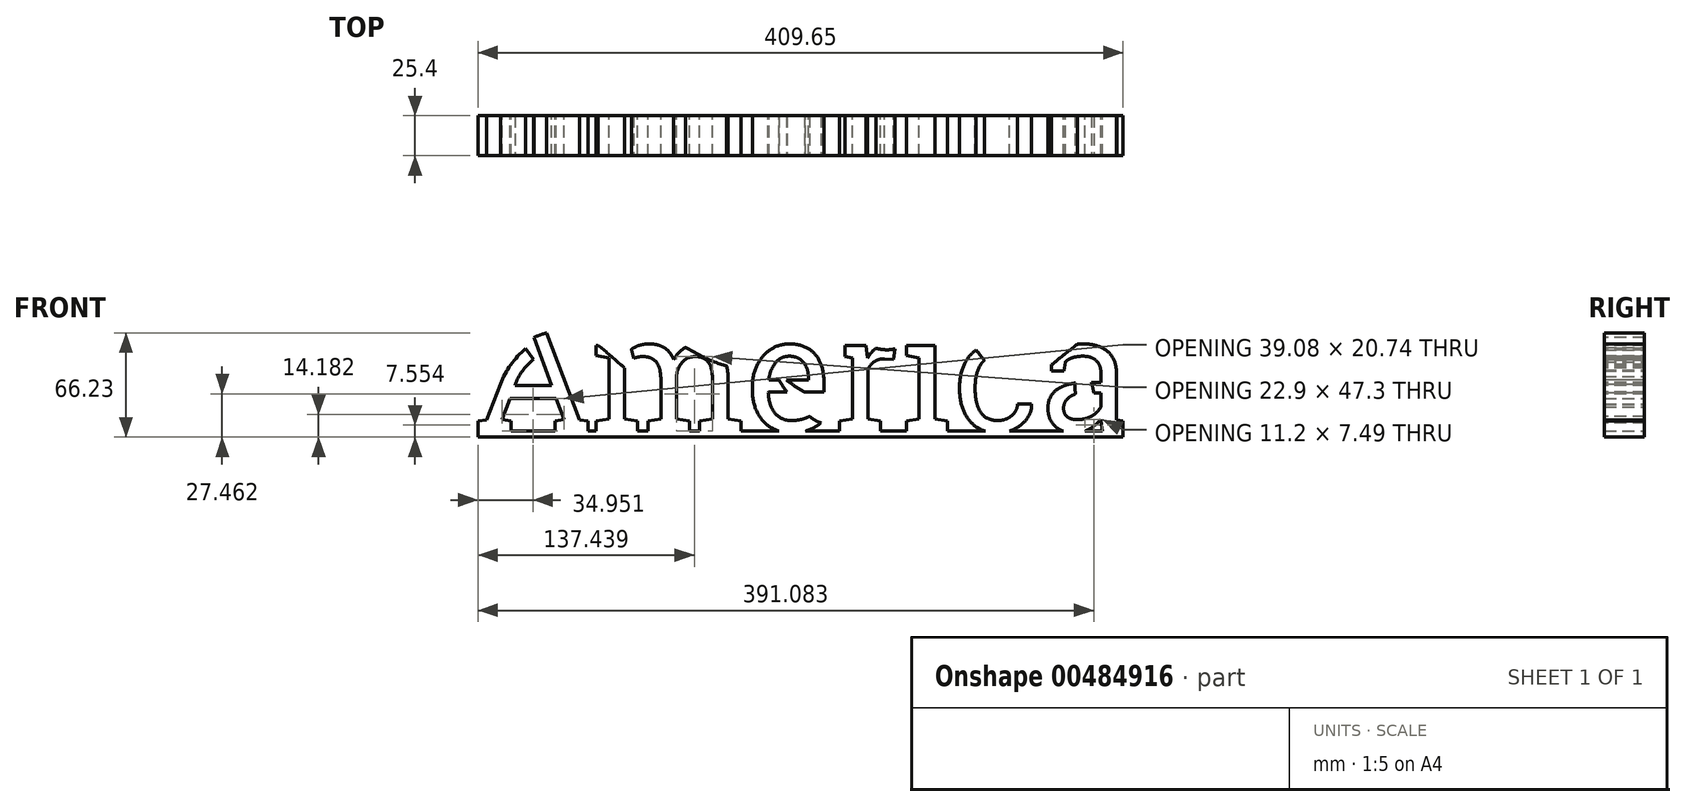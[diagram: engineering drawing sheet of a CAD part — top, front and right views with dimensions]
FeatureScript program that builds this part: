
annotation { "Feature Type Name" : "Feature", "Feature Type Description" : "" }
export const myFeature = defineFeature(function(context is Context, id is Id, definition is map)
    precondition{}
    {
        {
            var Q0;
            Q0=qCreatedBy(makeId("Front.planeOp"),FACE);
            var sketch = newSketch(context, id + "F0", { "sketchPlane" : qUnion([Q0])});
            skText(sketch, "E0", { "text": "America", "fontName": "RobotoSlab-Regular.ttf"});
            const initialGuessF0  = {"E0": [-0.10996, 0, 1, 0, 0.07404]};
            skSetInitialGuess(sketch, initialGuessF0);
            skSolve(sketch);
        }
        {
            var Q0;
            Q0 = qSketchRegion(id + "F0", true);
            extrude(context, id + "F1", {"entities" : qUnion([Q0]), "depth" : 25.4 * mm});
        }
        {
            var Q0;
            Q0=makeQuery(id+"F1.opExtrude","SWEPT_FACE",FACE,{"disambiguationData":[OSD([sQuery(id+"F0.wireOp",EDGE,"E0.sketch_text.stroke-14")])]});
            var sketch = newSketch(context, id + "F2", { "sketchPlane" : qUnion([Q0])});
            skLineSegment(sketch, "E1.bottom", {"start": v(-107.2, 25.4) * mm, "end": v(302.44, 25.4) * mm});
            skLineSegment(sketch, "E1.top", {"start": v(-107.2, 0) * mm, "end": v(302.44, 0) * mm});
            skLineSegment(sketch, "E1.left", {"start": v(-107.2, 25.4) * mm, "end": v(-107.2, 0) * mm});
            skLineSegment(sketch, "E1.right", {"start": v(302.44, 25.4) * mm, "end": v(302.44, 0) * mm});
            skSolve(sketch);
        }
        {
            var Q0;
            Q0 = qSketchRegion(id + "F2", true);
            extrude(context, id + "F3", {"entities" : qUnion([Q0]), "operationType" : NewBodyOperationType.ADD, "depth" : 3.8 * mm});
        }
        {
            var Q0;
            Q0=makeQuery(id+"F3.boolean.opBoolean","MERGE",FACE,{"derivedFrom":[makeQuery(id+"F1.opExtrude","CAP_FACE",FACE,{"disambiguationData":[OSD([sQuery(id+"F0.wireOp",EDGE,"E0.sketch_text.stroke-0"),sQuery(id+"F0.wireOp",EDGE,"E0.sketch_text.stroke-1"),sQuery(id+"F0.wireOp",EDGE,"E0.sketch_text.stroke-2"),sQuery(id+"F0.wireOp",EDGE,"E0.sketch_text.stroke-3"),sQuery(id+"F0.wireOp",EDGE,"E0.sketch_text.stroke-4"),sQuery(id+"F0.wireOp",EDGE,"E0.sketch_text.stroke-5"),sQuery(id+"F0.wireOp",EDGE,"E0.sketch_text.stroke-6"),sQuery(id+"F0.wireOp",EDGE,"E0.sketch_text.stroke-7"),sQuery(id+"F0.wireOp",EDGE,"E0.sketch_text.stroke-8"),sQuery(id+"F0.wireOp",EDGE,"E0.sketch_text.stroke-9"),sQuery(id+"F0.wireOp",EDGE,"E0.sketch_text.stroke-10"),sQuery(id+"F0.wireOp",EDGE,"E0.sketch_text.stroke-11"),sQuery(id+"F0.wireOp",EDGE,"E0.sketch_text.stroke-12"),sQuery(id+"F0.wireOp",EDGE,"E0.sketch_text.stroke-13"),sQuery(id+"F0.wireOp",EDGE,"E0.sketch_text.stroke-14"),sQuery(id+"F0.wireOp",EDGE,"E0.sketch_text.stroke-15"),sQuery(id+"F0.wireOp",EDGE,"E0.sketch_text.stroke-16"),sQuery(id+"F0.wireOp",EDGE,"E0.sketch_text.stroke-17"),sQuery(id+"F0.wireOp",EDGE,"E0.sketch_text.stroke-18"),sQuery(id+"F0.wireOp",EDGE,"E0.sketch_text.stroke-19")])],"isStart":false}),makeQuery(id+"F1.opExtrude","CAP_FACE",FACE,{"disambiguationData":[OSD([sQuery(id+"F0.wireOp",EDGE,"E0.sketch_text.stroke-20"),sQuery(id+"F0.wireOp",EDGE,"E0.sketch_text.stroke-21"),sQuery(id+"F0.wireOp",EDGE,"E0.sketch_text.stroke-22"),sQuery(id+"F0.wireOp",EDGE,"E0.sketch_text.stroke-23"),sQuery(id+"F0.wireOp",EDGE,"E0.sketch_text.stroke-24"),sQuery(id+"F0.wireOp",EDGE,"E0.sketch_text.stroke-25"),sQuery(id+"F0.wireOp",EDGE,"E0.sketch_text.stroke-26"),sQuery(id+"F0.wireOp",EDGE,"E0.sketch_text.stroke-27"),sQuery(id+"F0.wireOp",EDGE,"E0.sketch_text.stroke-28"),sQuery(id+"F0.wireOp",EDGE,"E0.sketch_text.stroke-29"),sQuery(id+"F0.wireOp",EDGE,"E0.sketch_text.stroke-30"),sQuery(id+"F0.wireOp",EDGE,"E0.sketch_text.stroke-31"),sQuery(id+"F0.wireOp",EDGE,"E0.sketch_text.stroke-32"),sQuery(id+"F0.wireOp",EDGE,"E0.sketch_text.stroke-33"),sQuery(id+"F0.wireOp",EDGE,"E0.sketch_text.stroke-34"),sQuery(id+"F0.wireOp",EDGE,"E0.sketch_text.stroke-35"),sQuery(id+"F0.wireOp",EDGE,"E0.sketch_text.stroke-36"),sQuery(id+"F0.wireOp",EDGE,"E0.sketch_text.stroke-37"),sQuery(id+"F0.wireOp",EDGE,"E0.sketch_text.stroke-38"),sQuery(id+"F0.wireOp",EDGE,"E0.sketch_text.stroke-39"),sQuery(id+"F0.wireOp",EDGE,"E0.sketch_text.stroke-40"),sQuery(id+"F0.wireOp",EDGE,"E0.sketch_text.stroke-41"),sQuery(id+"F0.wireOp",EDGE,"E0.sketch_text.stroke-42"),sQuery(id+"F0.wireOp",EDGE,"E0.sketch_text.stroke-43"),sQuery(id+"F0.wireOp",EDGE,"E0.sketch_text.stroke-44"),sQuery(id+"F0.wireOp",EDGE,"E0.sketch_text.stroke-45"),sQuery(id+"F0.wireOp",EDGE,"E0.sketch_text.stroke-46"),sQuery(id+"F0.wireOp",EDGE,"E0.sketch_text.stroke-47"),sQuery(id+"F0.wireOp",EDGE,"E0.sketch_text.stroke-48"),sQuery(id+"F0.wireOp",EDGE,"E0.sketch_text.stroke-49"),sQuery(id+"F0.wireOp",EDGE,"E0.sketch_text.stroke-50"),sQuery(id+"F0.wireOp",EDGE,"E0.sketch_text.stroke-51"),sQuery(id+"F0.wireOp",EDGE,"E0.sketch_text.stroke-52"),sQuery(id+"F0.wireOp",EDGE,"E0.sketch_text.stroke-53"),sQuery(id+"F0.wireOp",EDGE,"E0.sketch_text.stroke-54"),sQuery(id+"F0.wireOp",EDGE,"E0.sketch_text.stroke-55"),sQuery(id+"F0.wireOp",EDGE,"E0.sketch_text.stroke-56"),sQuery(id+"F0.wireOp",EDGE,"E0.sketch_text.stroke-57"),sQuery(id+"F0.wireOp",EDGE,"E0.sketch_text.stroke-58"),sQuery(id+"F0.wireOp",EDGE,"E0.sketch_text.stroke-59"),sQuery(id+"F0.wireOp",EDGE,"E0.sketch_text.stroke-60")])],"isStart":false}),makeQuery(id+"F1.opExtrude","CAP_FACE",FACE,{"disambiguationData":[OSD([sQuery(id+"F0.wireOp",EDGE,"E0.sketch_text.stroke-61"),sQuery(id+"F0.wireOp",EDGE,"E0.sketch_text.stroke-62"),sQuery(id+"F0.wireOp",EDGE,"E0.sketch_text.stroke-63"),sQuery(id+"F0.wireOp",EDGE,"E0.sketch_text.stroke-64"),sQuery(id+"F0.wireOp",EDGE,"E0.sketch_text.stroke-65"),sQuery(id+"F0.wireOp",EDGE,"E0.sketch_text.stroke-66"),sQuery(id+"F0.wireOp",EDGE,"E0.sketch_text.stroke-67"),sQuery(id+"F0.wireOp",EDGE,"E0.sketch_text.stroke-68"),sQuery(id+"F0.wireOp",EDGE,"E0.sketch_text.stroke-69"),sQuery(id+"F0.wireOp",EDGE,"E0.sketch_text.stroke-70"),sQuery(id+"F0.wireOp",EDGE,"E0.sketch_text.stroke-71"),sQuery(id+"F0.wireOp",EDGE,"E0.sketch_text.stroke-72"),sQuery(id+"F0.wireOp",EDGE,"E0.sketch_text.stroke-73"),sQuery(id+"F0.wireOp",EDGE,"E0.sketch_text.stroke-74"),sQuery(id+"F0.wireOp",EDGE,"E0.sketch_text.stroke-75"),sQuery(id+"F0.wireOp",EDGE,"E0.sketch_text.stroke-76"),sQuery(id+"F0.wireOp",EDGE,"E0.sketch_text.stroke-77"),sQuery(id+"F0.wireOp",EDGE,"E0.sketch_text.stroke-78"),sQuery(id+"F0.wireOp",EDGE,"E0.sketch_text.stroke-79"),sQuery(id+"F0.wireOp",EDGE,"E0.sketch_text.stroke-80"),sQuery(id+"F0.wireOp",EDGE,"E0.sketch_text.stroke-81"),sQuery(id+"F0.wireOp",EDGE,"E0.sketch_text.stroke-82"),sQuery(id+"F0.wireOp",EDGE,"E0.sketch_text.stroke-83"),sQuery(id+"F0.wireOp",EDGE,"E0.sketch_text.stroke-84")])],"isStart":false}),makeQuery(id+"F1.opExtrude","CAP_FACE",FACE,{"disambiguationData":[OSD([sQuery(id+"F0.wireOp",EDGE,"E0.sketch_text.stroke-85"),sQuery(id+"F0.wireOp",EDGE,"E0.sketch_text.stroke-86"),sQuery(id+"F0.wireOp",EDGE,"E0.sketch_text.stroke-87"),sQuery(id+"F0.wireOp",EDGE,"E0.sketch_text.stroke-88"),sQuery(id+"F0.wireOp",EDGE,"E0.sketch_text.stroke-89"),sQuery(id+"F0.wireOp",EDGE,"E0.sketch_text.stroke-90"),sQuery(id+"F0.wireOp",EDGE,"E0.sketch_text.stroke-91"),sQuery(id+"F0.wireOp",EDGE,"E0.sketch_text.stroke-92"),sQuery(id+"F0.wireOp",EDGE,"E0.sketch_text.stroke-93"),sQuery(id+"F0.wireOp",EDGE,"E0.sketch_text.stroke-94"),sQuery(id+"F0.wireOp",EDGE,"E0.sketch_text.stroke-95"),sQuery(id+"F0.wireOp",EDGE,"E0.sketch_text.stroke-96"),sQuery(id+"F0.wireOp",EDGE,"E0.sketch_text.stroke-97"),sQuery(id+"F0.wireOp",EDGE,"E0.sketch_text.stroke-98"),sQuery(id+"F0.wireOp",EDGE,"E0.sketch_text.stroke-99"),sQuery(id+"F0.wireOp",EDGE,"E0.sketch_text.stroke-100"),sQuery(id+"F0.wireOp",EDGE,"E0.sketch_text.stroke-101"),sQuery(id+"F0.wireOp",EDGE,"E0.sketch_text.stroke-102"),sQuery(id+"F0.wireOp",EDGE,"E0.sketch_text.stroke-103")])],"isStart":false}),makeQuery(id+"F1.opExtrude","CAP_FACE",FACE,{"disambiguationData":[OSD([sQuery(id+"F0.wireOp",EDGE,"E0.sketch_text.stroke-104"),sQuery(id+"F0.wireOp",EDGE,"E0.sketch_text.stroke-105"),sQuery(id+"F0.wireOp",EDGE,"E0.sketch_text.stroke-106"),sQuery(id+"F0.wireOp",EDGE,"E0.sketch_text.stroke-107"),sQuery(id+"F0.wireOp",EDGE,"E0.sketch_text.stroke-108"),sQuery(id+"F0.wireOp",EDGE,"E0.sketch_text.stroke-109"),sQuery(id+"F0.wireOp",EDGE,"E0.sketch_text.stroke-110"),sQuery(id+"F0.wireOp",EDGE,"E0.sketch_text.stroke-111"),sQuery(id+"F0.wireOp",EDGE,"E0.sketch_text.stroke-112"),sQuery(id+"F0.wireOp",EDGE,"E0.sketch_text.stroke-113")])],"isStart":false}),makeQuery(id+"F1.opExtrude","CAP_FACE",FACE,{"disambiguationData":[OSD([sQuery(id+"F0.wireOp",EDGE,"E0.sketch_text.stroke-118"),sQuery(id+"F0.wireOp",EDGE,"E0.sketch_text.stroke-119"),sQuery(id+"F0.wireOp",EDGE,"E0.sketch_text.stroke-120"),sQuery(id+"F0.wireOp",EDGE,"E0.sketch_text.stroke-121"),sQuery(id+"F0.wireOp",EDGE,"E0.sketch_text.stroke-122"),sQuery(id+"F0.wireOp",EDGE,"E0.sketch_text.stroke-123"),sQuery(id+"F0.wireOp",EDGE,"E0.sketch_text.stroke-124"),sQuery(id+"F0.wireOp",EDGE,"E0.sketch_text.stroke-125"),sQuery(id+"F0.wireOp",EDGE,"E0.sketch_text.stroke-126"),sQuery(id+"F0.wireOp",EDGE,"E0.sketch_text.stroke-127"),sQuery(id+"F0.wireOp",EDGE,"E0.sketch_text.stroke-128"),sQuery(id+"F0.wireOp",EDGE,"E0.sketch_text.stroke-129"),sQuery(id+"F0.wireOp",EDGE,"E0.sketch_text.stroke-130"),sQuery(id+"F0.wireOp",EDGE,"E0.sketch_text.stroke-131"),sQuery(id+"F0.wireOp",EDGE,"E0.sketch_text.stroke-132"),sQuery(id+"F0.wireOp",EDGE,"E0.sketch_text.stroke-133"),sQuery(id+"F0.wireOp",EDGE,"E0.sketch_text.stroke-134"),sQuery(id+"F0.wireOp",EDGE,"E0.sketch_text.stroke-135"),sQuery(id+"F0.wireOp",EDGE,"E0.sketch_text.stroke-136"),sQuery(id+"F0.wireOp",EDGE,"E0.sketch_text.stroke-137"),sQuery(id+"F0.wireOp",EDGE,"E0.sketch_text.stroke-138"),sQuery(id+"F0.wireOp",EDGE,"E0.sketch_text.stroke-139"),sQuery(id+"F0.wireOp",EDGE,"E0.sketch_text.stroke-140")])],"isStart":false}),makeQuery(id+"F1.opExtrude","CAP_FACE",FACE,{"disambiguationData":[OSD([sQuery(id+"F0.wireOp",EDGE,"E0.sketch_text.stroke-141"),sQuery(id+"F0.wireOp",EDGE,"E0.sketch_text.stroke-142"),sQuery(id+"F0.wireOp",EDGE,"E0.sketch_text.stroke-143"),sQuery(id+"F0.wireOp",EDGE,"E0.sketch_text.stroke-144"),sQuery(id+"F0.wireOp",EDGE,"E0.sketch_text.stroke-145"),sQuery(id+"F0.wireOp",EDGE,"E0.sketch_text.stroke-146"),sQuery(id+"F0.wireOp",EDGE,"E0.sketch_text.stroke-147"),sQuery(id+"F0.wireOp",EDGE,"E0.sketch_text.stroke-148"),sQuery(id+"F0.wireOp",EDGE,"E0.sketch_text.stroke-149"),sQuery(id+"F0.wireOp",EDGE,"E0.sketch_text.stroke-150"),sQuery(id+"F0.wireOp",EDGE,"E0.sketch_text.stroke-151"),sQuery(id+"F0.wireOp",EDGE,"E0.sketch_text.stroke-152"),sQuery(id+"F0.wireOp",EDGE,"E0.sketch_text.stroke-153"),sQuery(id+"F0.wireOp",EDGE,"E0.sketch_text.stroke-154"),sQuery(id+"F0.wireOp",EDGE,"E0.sketch_text.stroke-155"),sQuery(id+"F0.wireOp",EDGE,"E0.sketch_text.stroke-156"),sQuery(id+"F0.wireOp",EDGE,"E0.sketch_text.stroke-157"),sQuery(id+"F0.wireOp",EDGE,"E0.sketch_text.stroke-158"),sQuery(id+"F0.wireOp",EDGE,"E0.sketch_text.stroke-159"),sQuery(id+"F0.wireOp",EDGE,"E0.sketch_text.stroke-160"),sQuery(id+"F0.wireOp",EDGE,"E0.sketch_text.stroke-161"),sQuery(id+"F0.wireOp",EDGE,"E0.sketch_text.stroke-162"),sQuery(id+"F0.wireOp",EDGE,"E0.sketch_text.stroke-163"),sQuery(id+"F0.wireOp",EDGE,"E0.sketch_text.stroke-164"),sQuery(id+"F0.wireOp",EDGE,"E0.sketch_text.stroke-165"),sQuery(id+"F0.wireOp",EDGE,"E0.sketch_text.stroke-166"),sQuery(id+"F0.wireOp",EDGE,"E0.sketch_text.stroke-167"),sQuery(id+"F0.wireOp",EDGE,"E0.sketch_text.stroke-168"),sQuery(id+"F0.wireOp",EDGE,"E0.sketch_text.stroke-169"),sQuery(id+"F0.wireOp",EDGE,"E0.sketch_text.stroke-170"),sQuery(id+"F0.wireOp",EDGE,"E0.sketch_text.stroke-171"),sQuery(id+"F0.wireOp",EDGE,"E0.sketch_text.stroke-172"),sQuery(id+"F0.wireOp",EDGE,"E0.sketch_text.stroke-173"),sQuery(id+"F0.wireOp",EDGE,"E0.sketch_text.stroke-174"),sQuery(id+"F0.wireOp",EDGE,"E0.sketch_text.stroke-175")])],"isStart":false}),makeQuery(id+"F3.opExtrude","SWEPT_FACE",FACE,{"disambiguationData":[OSD([sQuery(id+"F2.wireOp",EDGE,"E1.bottom")])]})]});
            var sketch = newSketch(context, id + "F4", { "sketchPlane" : qUnion([Q0])});
            skFitSpline(sketch, "E2", {"points": [v(-100.8, 53.9) * mm, v(-46.48, 63.1) * mm, v(-6.63, 35.95) * mm, v(-11.01, 68.8) * mm, v(58.62, 40.33) * mm, v(96.29, 68.36) * mm, v(154.97, 51.72) * mm, v(190, 67.92) * mm, v(230.3, 27.63) * mm, v(248.7, 35.07) * mm, v(294.43, 72.4) * mm, v(304.52, 101.14) * mm, v(-135.8, 109.68) * mm, v(-100.8, 53.9) * mm]});
            skSolve(sketch);
        }
        {
            var Q0;
            Q0 = qSketchRegion(id + "F4", true);
            extrude(context, id + "F5", {"entities" : qUnion([Q0]), "operationType" : NewBodyOperationType.REMOVE, "endBound" : BoundingType.THROUGH_ALL, "oppositeDirection" : true, "depth" : 25.4 * mm});
        }
        {
            var Q0;
            Q0=makeQuery(id+"F3.boolean.opBoolean","MERGE",FACE,{"derivedFrom":[makeQuery(id+"F1.opExtrude","CAP_FACE",FACE,{"disambiguationData":[OSD([sQuery(id+"F0.wireOp",EDGE,"E0.sketch_text.stroke-0"),sQuery(id+"F0.wireOp",EDGE,"E0.sketch_text.stroke-1"),sQuery(id+"F0.wireOp",EDGE,"E0.sketch_text.stroke-2"),sQuery(id+"F0.wireOp",EDGE,"E0.sketch_text.stroke-3"),sQuery(id+"F0.wireOp",EDGE,"E0.sketch_text.stroke-4"),sQuery(id+"F0.wireOp",EDGE,"E0.sketch_text.stroke-5"),sQuery(id+"F0.wireOp",EDGE,"E0.sketch_text.stroke-6"),sQuery(id+"F0.wireOp",EDGE,"E0.sketch_text.stroke-7"),sQuery(id+"F0.wireOp",EDGE,"E0.sketch_text.stroke-8"),sQuery(id+"F0.wireOp",EDGE,"E0.sketch_text.stroke-9"),sQuery(id+"F0.wireOp",EDGE,"E0.sketch_text.stroke-10"),sQuery(id+"F0.wireOp",EDGE,"E0.sketch_text.stroke-11"),sQuery(id+"F0.wireOp",EDGE,"E0.sketch_text.stroke-12"),sQuery(id+"F0.wireOp",EDGE,"E0.sketch_text.stroke-13"),sQuery(id+"F0.wireOp",EDGE,"E0.sketch_text.stroke-14"),sQuery(id+"F0.wireOp",EDGE,"E0.sketch_text.stroke-15"),sQuery(id+"F0.wireOp",EDGE,"E0.sketch_text.stroke-16"),sQuery(id+"F0.wireOp",EDGE,"E0.sketch_text.stroke-17"),sQuery(id+"F0.wireOp",EDGE,"E0.sketch_text.stroke-18"),sQuery(id+"F0.wireOp",EDGE,"E0.sketch_text.stroke-19")])],"isStart":false}),makeQuery(id+"F1.opExtrude","CAP_FACE",FACE,{"disambiguationData":[OSD([sQuery(id+"F0.wireOp",EDGE,"E0.sketch_text.stroke-20"),sQuery(id+"F0.wireOp",EDGE,"E0.sketch_text.stroke-21"),sQuery(id+"F0.wireOp",EDGE,"E0.sketch_text.stroke-22"),sQuery(id+"F0.wireOp",EDGE,"E0.sketch_text.stroke-23"),sQuery(id+"F0.wireOp",EDGE,"E0.sketch_text.stroke-24"),sQuery(id+"F0.wireOp",EDGE,"E0.sketch_text.stroke-25"),sQuery(id+"F0.wireOp",EDGE,"E0.sketch_text.stroke-26"),sQuery(id+"F0.wireOp",EDGE,"E0.sketch_text.stroke-27"),sQuery(id+"F0.wireOp",EDGE,"E0.sketch_text.stroke-28"),sQuery(id+"F0.wireOp",EDGE,"E0.sketch_text.stroke-29"),sQuery(id+"F0.wireOp",EDGE,"E0.sketch_text.stroke-30"),sQuery(id+"F0.wireOp",EDGE,"E0.sketch_text.stroke-31"),sQuery(id+"F0.wireOp",EDGE,"E0.sketch_text.stroke-32"),sQuery(id+"F0.wireOp",EDGE,"E0.sketch_text.stroke-33"),sQuery(id+"F0.wireOp",EDGE,"E0.sketch_text.stroke-34"),sQuery(id+"F0.wireOp",EDGE,"E0.sketch_text.stroke-35"),sQuery(id+"F0.wireOp",EDGE,"E0.sketch_text.stroke-36"),sQuery(id+"F0.wireOp",EDGE,"E0.sketch_text.stroke-37"),sQuery(id+"F0.wireOp",EDGE,"E0.sketch_text.stroke-38"),sQuery(id+"F0.wireOp",EDGE,"E0.sketch_text.stroke-39"),sQuery(id+"F0.wireOp",EDGE,"E0.sketch_text.stroke-40"),sQuery(id+"F0.wireOp",EDGE,"E0.sketch_text.stroke-41"),sQuery(id+"F0.wireOp",EDGE,"E0.sketch_text.stroke-42"),sQuery(id+"F0.wireOp",EDGE,"E0.sketch_text.stroke-43"),sQuery(id+"F0.wireOp",EDGE,"E0.sketch_text.stroke-44"),sQuery(id+"F0.wireOp",EDGE,"E0.sketch_text.stroke-45"),sQuery(id+"F0.wireOp",EDGE,"E0.sketch_text.stroke-46"),sQuery(id+"F0.wireOp",EDGE,"E0.sketch_text.stroke-47"),sQuery(id+"F0.wireOp",EDGE,"E0.sketch_text.stroke-48"),sQuery(id+"F0.wireOp",EDGE,"E0.sketch_text.stroke-49"),sQuery(id+"F0.wireOp",EDGE,"E0.sketch_text.stroke-50"),sQuery(id+"F0.wireOp",EDGE,"E0.sketch_text.stroke-51"),sQuery(id+"F0.wireOp",EDGE,"E0.sketch_text.stroke-52"),sQuery(id+"F0.wireOp",EDGE,"E0.sketch_text.stroke-53"),sQuery(id+"F0.wireOp",EDGE,"E0.sketch_text.stroke-54"),sQuery(id+"F0.wireOp",EDGE,"E0.sketch_text.stroke-55"),sQuery(id+"F0.wireOp",EDGE,"E0.sketch_text.stroke-56"),sQuery(id+"F0.wireOp",EDGE,"E0.sketch_text.stroke-57"),sQuery(id+"F0.wireOp",EDGE,"E0.sketch_text.stroke-58"),sQuery(id+"F0.wireOp",EDGE,"E0.sketch_text.stroke-59"),sQuery(id+"F0.wireOp",EDGE,"E0.sketch_text.stroke-60")])],"isStart":false}),makeQuery(id+"F1.opExtrude","CAP_FACE",FACE,{"disambiguationData":[OSD([sQuery(id+"F0.wireOp",EDGE,"E0.sketch_text.stroke-61"),sQuery(id+"F0.wireOp",EDGE,"E0.sketch_text.stroke-62"),sQuery(id+"F0.wireOp",EDGE,"E0.sketch_text.stroke-63"),sQuery(id+"F0.wireOp",EDGE,"E0.sketch_text.stroke-64"),sQuery(id+"F0.wireOp",EDGE,"E0.sketch_text.stroke-65"),sQuery(id+"F0.wireOp",EDGE,"E0.sketch_text.stroke-66"),sQuery(id+"F0.wireOp",EDGE,"E0.sketch_text.stroke-67"),sQuery(id+"F0.wireOp",EDGE,"E0.sketch_text.stroke-68"),sQuery(id+"F0.wireOp",EDGE,"E0.sketch_text.stroke-69"),sQuery(id+"F0.wireOp",EDGE,"E0.sketch_text.stroke-70"),sQuery(id+"F0.wireOp",EDGE,"E0.sketch_text.stroke-71"),sQuery(id+"F0.wireOp",EDGE,"E0.sketch_text.stroke-72"),sQuery(id+"F0.wireOp",EDGE,"E0.sketch_text.stroke-73"),sQuery(id+"F0.wireOp",EDGE,"E0.sketch_text.stroke-74"),sQuery(id+"F0.wireOp",EDGE,"E0.sketch_text.stroke-75"),sQuery(id+"F0.wireOp",EDGE,"E0.sketch_text.stroke-76"),sQuery(id+"F0.wireOp",EDGE,"E0.sketch_text.stroke-77"),sQuery(id+"F0.wireOp",EDGE,"E0.sketch_text.stroke-78"),sQuery(id+"F0.wireOp",EDGE,"E0.sketch_text.stroke-79"),sQuery(id+"F0.wireOp",EDGE,"E0.sketch_text.stroke-80"),sQuery(id+"F0.wireOp",EDGE,"E0.sketch_text.stroke-81"),sQuery(id+"F0.wireOp",EDGE,"E0.sketch_text.stroke-82"),sQuery(id+"F0.wireOp",EDGE,"E0.sketch_text.stroke-83"),sQuery(id+"F0.wireOp",EDGE,"E0.sketch_text.stroke-84")])],"isStart":false}),makeQuery(id+"F1.opExtrude","CAP_FACE",FACE,{"disambiguationData":[OSD([sQuery(id+"F0.wireOp",EDGE,"E0.sketch_text.stroke-85"),sQuery(id+"F0.wireOp",EDGE,"E0.sketch_text.stroke-86"),sQuery(id+"F0.wireOp",EDGE,"E0.sketch_text.stroke-87"),sQuery(id+"F0.wireOp",EDGE,"E0.sketch_text.stroke-88"),sQuery(id+"F0.wireOp",EDGE,"E0.sketch_text.stroke-89"),sQuery(id+"F0.wireOp",EDGE,"E0.sketch_text.stroke-90"),sQuery(id+"F0.wireOp",EDGE,"E0.sketch_text.stroke-91"),sQuery(id+"F0.wireOp",EDGE,"E0.sketch_text.stroke-92"),sQuery(id+"F0.wireOp",EDGE,"E0.sketch_text.stroke-93"),sQuery(id+"F0.wireOp",EDGE,"E0.sketch_text.stroke-94"),sQuery(id+"F0.wireOp",EDGE,"E0.sketch_text.stroke-95"),sQuery(id+"F0.wireOp",EDGE,"E0.sketch_text.stroke-96"),sQuery(id+"F0.wireOp",EDGE,"E0.sketch_text.stroke-97"),sQuery(id+"F0.wireOp",EDGE,"E0.sketch_text.stroke-98"),sQuery(id+"F0.wireOp",EDGE,"E0.sketch_text.stroke-99"),sQuery(id+"F0.wireOp",EDGE,"E0.sketch_text.stroke-100"),sQuery(id+"F0.wireOp",EDGE,"E0.sketch_text.stroke-101"),sQuery(id+"F0.wireOp",EDGE,"E0.sketch_text.stroke-102"),sQuery(id+"F0.wireOp",EDGE,"E0.sketch_text.stroke-103")])],"isStart":false}),makeQuery(id+"F1.opExtrude","CAP_FACE",FACE,{"disambiguationData":[OSD([sQuery(id+"F0.wireOp",EDGE,"E0.sketch_text.stroke-104"),sQuery(id+"F0.wireOp",EDGE,"E0.sketch_text.stroke-105"),sQuery(id+"F0.wireOp",EDGE,"E0.sketch_text.stroke-106"),sQuery(id+"F0.wireOp",EDGE,"E0.sketch_text.stroke-107"),sQuery(id+"F0.wireOp",EDGE,"E0.sketch_text.stroke-108"),sQuery(id+"F0.wireOp",EDGE,"E0.sketch_text.stroke-109"),sQuery(id+"F0.wireOp",EDGE,"E0.sketch_text.stroke-110"),sQuery(id+"F0.wireOp",EDGE,"E0.sketch_text.stroke-111"),sQuery(id+"F0.wireOp",EDGE,"E0.sketch_text.stroke-112"),sQuery(id+"F0.wireOp",EDGE,"E0.sketch_text.stroke-113")])],"isStart":false}),makeQuery(id+"F1.opExtrude","CAP_FACE",FACE,{"disambiguationData":[OSD([sQuery(id+"F0.wireOp",EDGE,"E0.sketch_text.stroke-118"),sQuery(id+"F0.wireOp",EDGE,"E0.sketch_text.stroke-119"),sQuery(id+"F0.wireOp",EDGE,"E0.sketch_text.stroke-120"),sQuery(id+"F0.wireOp",EDGE,"E0.sketch_text.stroke-121"),sQuery(id+"F0.wireOp",EDGE,"E0.sketch_text.stroke-122"),sQuery(id+"F0.wireOp",EDGE,"E0.sketch_text.stroke-123"),sQuery(id+"F0.wireOp",EDGE,"E0.sketch_text.stroke-124"),sQuery(id+"F0.wireOp",EDGE,"E0.sketch_text.stroke-125"),sQuery(id+"F0.wireOp",EDGE,"E0.sketch_text.stroke-126"),sQuery(id+"F0.wireOp",EDGE,"E0.sketch_text.stroke-127"),sQuery(id+"F0.wireOp",EDGE,"E0.sketch_text.stroke-128"),sQuery(id+"F0.wireOp",EDGE,"E0.sketch_text.stroke-129"),sQuery(id+"F0.wireOp",EDGE,"E0.sketch_text.stroke-130"),sQuery(id+"F0.wireOp",EDGE,"E0.sketch_text.stroke-131"),sQuery(id+"F0.wireOp",EDGE,"E0.sketch_text.stroke-132"),sQuery(id+"F0.wireOp",EDGE,"E0.sketch_text.stroke-133"),sQuery(id+"F0.wireOp",EDGE,"E0.sketch_text.stroke-134"),sQuery(id+"F0.wireOp",EDGE,"E0.sketch_text.stroke-135"),sQuery(id+"F0.wireOp",EDGE,"E0.sketch_text.stroke-136"),sQuery(id+"F0.wireOp",EDGE,"E0.sketch_text.stroke-137"),sQuery(id+"F0.wireOp",EDGE,"E0.sketch_text.stroke-138"),sQuery(id+"F0.wireOp",EDGE,"E0.sketch_text.stroke-139"),sQuery(id+"F0.wireOp",EDGE,"E0.sketch_text.stroke-140")])],"isStart":false}),makeQuery(id+"F1.opExtrude","CAP_FACE",FACE,{"disambiguationData":[OSD([sQuery(id+"F0.wireOp",EDGE,"E0.sketch_text.stroke-141"),sQuery(id+"F0.wireOp",EDGE,"E0.sketch_text.stroke-142"),sQuery(id+"F0.wireOp",EDGE,"E0.sketch_text.stroke-143"),sQuery(id+"F0.wireOp",EDGE,"E0.sketch_text.stroke-144"),sQuery(id+"F0.wireOp",EDGE,"E0.sketch_text.stroke-145"),sQuery(id+"F0.wireOp",EDGE,"E0.sketch_text.stroke-146"),sQuery(id+"F0.wireOp",EDGE,"E0.sketch_text.stroke-147"),sQuery(id+"F0.wireOp",EDGE,"E0.sketch_text.stroke-148"),sQuery(id+"F0.wireOp",EDGE,"E0.sketch_text.stroke-149"),sQuery(id+"F0.wireOp",EDGE,"E0.sketch_text.stroke-150"),sQuery(id+"F0.wireOp",EDGE,"E0.sketch_text.stroke-151"),sQuery(id+"F0.wireOp",EDGE,"E0.sketch_text.stroke-152"),sQuery(id+"F0.wireOp",EDGE,"E0.sketch_text.stroke-153"),sQuery(id+"F0.wireOp",EDGE,"E0.sketch_text.stroke-154"),sQuery(id+"F0.wireOp",EDGE,"E0.sketch_text.stroke-155"),sQuery(id+"F0.wireOp",EDGE,"E0.sketch_text.stroke-156"),sQuery(id+"F0.wireOp",EDGE,"E0.sketch_text.stroke-157"),sQuery(id+"F0.wireOp",EDGE,"E0.sketch_text.stroke-158"),sQuery(id+"F0.wireOp",EDGE,"E0.sketch_text.stroke-159"),sQuery(id+"F0.wireOp",EDGE,"E0.sketch_text.stroke-160"),sQuery(id+"F0.wireOp",EDGE,"E0.sketch_text.stroke-161"),sQuery(id+"F0.wireOp",EDGE,"E0.sketch_text.stroke-162"),sQuery(id+"F0.wireOp",EDGE,"E0.sketch_text.stroke-163"),sQuery(id+"F0.wireOp",EDGE,"E0.sketch_text.stroke-164"),sQuery(id+"F0.wireOp",EDGE,"E0.sketch_text.stroke-165"),sQuery(id+"F0.wireOp",EDGE,"E0.sketch_text.stroke-166"),sQuery(id+"F0.wireOp",EDGE,"E0.sketch_text.stroke-167"),sQuery(id+"F0.wireOp",EDGE,"E0.sketch_text.stroke-168"),sQuery(id+"F0.wireOp",EDGE,"E0.sketch_text.stroke-169"),sQuery(id+"F0.wireOp",EDGE,"E0.sketch_text.stroke-170"),sQuery(id+"F0.wireOp",EDGE,"E0.sketch_text.stroke-171"),sQuery(id+"F0.wireOp",EDGE,"E0.sketch_text.stroke-172"),sQuery(id+"F0.wireOp",EDGE,"E0.sketch_text.stroke-173"),sQuery(id+"F0.wireOp",EDGE,"E0.sketch_text.stroke-174"),sQuery(id+"F0.wireOp",EDGE,"E0.sketch_text.stroke-175")])],"isStart":false}),makeQuery(id+"F3.opExtrude","SWEPT_FACE",FACE,{"disambiguationData":[OSD([sQuery(id+"F2.wireOp",EDGE,"E1.bottom")])]})]});
            var sketch = newSketch(context, id + "F6", { "sketchPlane" : qUnion([Q0])});
            skFitSpline(sketch, "E3", {"points": [v(111.72, 23.45) * mm, v(82.4, 36.55) * mm, v(115.34, 5.4) * mm, v(122.81, 107.96) * mm, v(111.72, 23.45) * mm]});
            skSolve(sketch);
        }
        {
            var Q0;
            Q0 = qSketchRegion(id + "F6", true);
            extrude(context, id + "F7", {"entities" : qUnion([Q0]), "operationType" : NewBodyOperationType.REMOVE, "endBound" : BoundingType.THROUGH_ALL, "oppositeDirection" : true, "depth" : 25.4 * mm});
        }
        {
            var Q0;
            Q0=makeQuery(id+"F3.boolean.opBoolean","MERGE",FACE,{"derivedFrom":[makeQuery(id+"F1.opExtrude","CAP_FACE",FACE,{"disambiguationData":[OSD([sQuery(id+"F0.wireOp",EDGE,"E0.sketch_text.stroke-0"),sQuery(id+"F0.wireOp",EDGE,"E0.sketch_text.stroke-1"),sQuery(id+"F0.wireOp",EDGE,"E0.sketch_text.stroke-2"),sQuery(id+"F0.wireOp",EDGE,"E0.sketch_text.stroke-3"),sQuery(id+"F0.wireOp",EDGE,"E0.sketch_text.stroke-4"),sQuery(id+"F0.wireOp",EDGE,"E0.sketch_text.stroke-5"),sQuery(id+"F0.wireOp",EDGE,"E0.sketch_text.stroke-6"),sQuery(id+"F0.wireOp",EDGE,"E0.sketch_text.stroke-7"),sQuery(id+"F0.wireOp",EDGE,"E0.sketch_text.stroke-8"),sQuery(id+"F0.wireOp",EDGE,"E0.sketch_text.stroke-9"),sQuery(id+"F0.wireOp",EDGE,"E0.sketch_text.stroke-10"),sQuery(id+"F0.wireOp",EDGE,"E0.sketch_text.stroke-11"),sQuery(id+"F0.wireOp",EDGE,"E0.sketch_text.stroke-12"),sQuery(id+"F0.wireOp",EDGE,"E0.sketch_text.stroke-13"),sQuery(id+"F0.wireOp",EDGE,"E0.sketch_text.stroke-14"),sQuery(id+"F0.wireOp",EDGE,"E0.sketch_text.stroke-15"),sQuery(id+"F0.wireOp",EDGE,"E0.sketch_text.stroke-16"),sQuery(id+"F0.wireOp",EDGE,"E0.sketch_text.stroke-17"),sQuery(id+"F0.wireOp",EDGE,"E0.sketch_text.stroke-18"),sQuery(id+"F0.wireOp",EDGE,"E0.sketch_text.stroke-19")])],"isStart":false}),makeQuery(id+"F1.opExtrude","CAP_FACE",FACE,{"disambiguationData":[OSD([sQuery(id+"F0.wireOp",EDGE,"E0.sketch_text.stroke-20"),sQuery(id+"F0.wireOp",EDGE,"E0.sketch_text.stroke-21"),sQuery(id+"F0.wireOp",EDGE,"E0.sketch_text.stroke-22"),sQuery(id+"F0.wireOp",EDGE,"E0.sketch_text.stroke-23"),sQuery(id+"F0.wireOp",EDGE,"E0.sketch_text.stroke-24"),sQuery(id+"F0.wireOp",EDGE,"E0.sketch_text.stroke-25"),sQuery(id+"F0.wireOp",EDGE,"E0.sketch_text.stroke-26"),sQuery(id+"F0.wireOp",EDGE,"E0.sketch_text.stroke-27"),sQuery(id+"F0.wireOp",EDGE,"E0.sketch_text.stroke-28"),sQuery(id+"F0.wireOp",EDGE,"E0.sketch_text.stroke-29"),sQuery(id+"F0.wireOp",EDGE,"E0.sketch_text.stroke-30"),sQuery(id+"F0.wireOp",EDGE,"E0.sketch_text.stroke-31"),sQuery(id+"F0.wireOp",EDGE,"E0.sketch_text.stroke-32"),sQuery(id+"F0.wireOp",EDGE,"E0.sketch_text.stroke-33"),sQuery(id+"F0.wireOp",EDGE,"E0.sketch_text.stroke-34"),sQuery(id+"F0.wireOp",EDGE,"E0.sketch_text.stroke-35"),sQuery(id+"F0.wireOp",EDGE,"E0.sketch_text.stroke-36"),sQuery(id+"F0.wireOp",EDGE,"E0.sketch_text.stroke-37"),sQuery(id+"F0.wireOp",EDGE,"E0.sketch_text.stroke-38"),sQuery(id+"F0.wireOp",EDGE,"E0.sketch_text.stroke-39"),sQuery(id+"F0.wireOp",EDGE,"E0.sketch_text.stroke-40"),sQuery(id+"F0.wireOp",EDGE,"E0.sketch_text.stroke-41"),sQuery(id+"F0.wireOp",EDGE,"E0.sketch_text.stroke-42"),sQuery(id+"F0.wireOp",EDGE,"E0.sketch_text.stroke-43"),sQuery(id+"F0.wireOp",EDGE,"E0.sketch_text.stroke-44"),sQuery(id+"F0.wireOp",EDGE,"E0.sketch_text.stroke-45"),sQuery(id+"F0.wireOp",EDGE,"E0.sketch_text.stroke-46"),sQuery(id+"F0.wireOp",EDGE,"E0.sketch_text.stroke-47"),sQuery(id+"F0.wireOp",EDGE,"E0.sketch_text.stroke-48"),sQuery(id+"F0.wireOp",EDGE,"E0.sketch_text.stroke-49"),sQuery(id+"F0.wireOp",EDGE,"E0.sketch_text.stroke-50"),sQuery(id+"F0.wireOp",EDGE,"E0.sketch_text.stroke-51"),sQuery(id+"F0.wireOp",EDGE,"E0.sketch_text.stroke-52"),sQuery(id+"F0.wireOp",EDGE,"E0.sketch_text.stroke-53"),sQuery(id+"F0.wireOp",EDGE,"E0.sketch_text.stroke-54"),sQuery(id+"F0.wireOp",EDGE,"E0.sketch_text.stroke-55"),sQuery(id+"F0.wireOp",EDGE,"E0.sketch_text.stroke-56"),sQuery(id+"F0.wireOp",EDGE,"E0.sketch_text.stroke-57"),sQuery(id+"F0.wireOp",EDGE,"E0.sketch_text.stroke-58"),sQuery(id+"F0.wireOp",EDGE,"E0.sketch_text.stroke-59"),sQuery(id+"F0.wireOp",EDGE,"E0.sketch_text.stroke-60")])],"isStart":false}),makeQuery(id+"F1.opExtrude","CAP_FACE",FACE,{"disambiguationData":[OSD([sQuery(id+"F0.wireOp",EDGE,"E0.sketch_text.stroke-61"),sQuery(id+"F0.wireOp",EDGE,"E0.sketch_text.stroke-62"),sQuery(id+"F0.wireOp",EDGE,"E0.sketch_text.stroke-63"),sQuery(id+"F0.wireOp",EDGE,"E0.sketch_text.stroke-64"),sQuery(id+"F0.wireOp",EDGE,"E0.sketch_text.stroke-65"),sQuery(id+"F0.wireOp",EDGE,"E0.sketch_text.stroke-66"),sQuery(id+"F0.wireOp",EDGE,"E0.sketch_text.stroke-67"),sQuery(id+"F0.wireOp",EDGE,"E0.sketch_text.stroke-68"),sQuery(id+"F0.wireOp",EDGE,"E0.sketch_text.stroke-69"),sQuery(id+"F0.wireOp",EDGE,"E0.sketch_text.stroke-70"),sQuery(id+"F0.wireOp",EDGE,"E0.sketch_text.stroke-71"),sQuery(id+"F0.wireOp",EDGE,"E0.sketch_text.stroke-72"),sQuery(id+"F0.wireOp",EDGE,"E0.sketch_text.stroke-73"),sQuery(id+"F0.wireOp",EDGE,"E0.sketch_text.stroke-74"),sQuery(id+"F0.wireOp",EDGE,"E0.sketch_text.stroke-75"),sQuery(id+"F0.wireOp",EDGE,"E0.sketch_text.stroke-76"),sQuery(id+"F0.wireOp",EDGE,"E0.sketch_text.stroke-77"),sQuery(id+"F0.wireOp",EDGE,"E0.sketch_text.stroke-78"),sQuery(id+"F0.wireOp",EDGE,"E0.sketch_text.stroke-79"),sQuery(id+"F0.wireOp",EDGE,"E0.sketch_text.stroke-80"),sQuery(id+"F0.wireOp",EDGE,"E0.sketch_text.stroke-81"),sQuery(id+"F0.wireOp",EDGE,"E0.sketch_text.stroke-82"),sQuery(id+"F0.wireOp",EDGE,"E0.sketch_text.stroke-83"),sQuery(id+"F0.wireOp",EDGE,"E0.sketch_text.stroke-84")])],"isStart":false}),makeQuery(id+"F1.opExtrude","CAP_FACE",FACE,{"disambiguationData":[OSD([sQuery(id+"F0.wireOp",EDGE,"E0.sketch_text.stroke-85"),sQuery(id+"F0.wireOp",EDGE,"E0.sketch_text.stroke-86"),sQuery(id+"F0.wireOp",EDGE,"E0.sketch_text.stroke-87"),sQuery(id+"F0.wireOp",EDGE,"E0.sketch_text.stroke-88"),sQuery(id+"F0.wireOp",EDGE,"E0.sketch_text.stroke-89"),sQuery(id+"F0.wireOp",EDGE,"E0.sketch_text.stroke-90"),sQuery(id+"F0.wireOp",EDGE,"E0.sketch_text.stroke-91"),sQuery(id+"F0.wireOp",EDGE,"E0.sketch_text.stroke-92"),sQuery(id+"F0.wireOp",EDGE,"E0.sketch_text.stroke-93"),sQuery(id+"F0.wireOp",EDGE,"E0.sketch_text.stroke-94"),sQuery(id+"F0.wireOp",EDGE,"E0.sketch_text.stroke-95"),sQuery(id+"F0.wireOp",EDGE,"E0.sketch_text.stroke-96"),sQuery(id+"F0.wireOp",EDGE,"E0.sketch_text.stroke-97"),sQuery(id+"F0.wireOp",EDGE,"E0.sketch_text.stroke-98"),sQuery(id+"F0.wireOp",EDGE,"E0.sketch_text.stroke-99"),sQuery(id+"F0.wireOp",EDGE,"E0.sketch_text.stroke-100"),sQuery(id+"F0.wireOp",EDGE,"E0.sketch_text.stroke-101"),sQuery(id+"F0.wireOp",EDGE,"E0.sketch_text.stroke-102"),sQuery(id+"F0.wireOp",EDGE,"E0.sketch_text.stroke-103")])],"isStart":false}),makeQuery(id+"F1.opExtrude","CAP_FACE",FACE,{"disambiguationData":[OSD([sQuery(id+"F0.wireOp",EDGE,"E0.sketch_text.stroke-104"),sQuery(id+"F0.wireOp",EDGE,"E0.sketch_text.stroke-105"),sQuery(id+"F0.wireOp",EDGE,"E0.sketch_text.stroke-106"),sQuery(id+"F0.wireOp",EDGE,"E0.sketch_text.stroke-107"),sQuery(id+"F0.wireOp",EDGE,"E0.sketch_text.stroke-108"),sQuery(id+"F0.wireOp",EDGE,"E0.sketch_text.stroke-109"),sQuery(id+"F0.wireOp",EDGE,"E0.sketch_text.stroke-110"),sQuery(id+"F0.wireOp",EDGE,"E0.sketch_text.stroke-111"),sQuery(id+"F0.wireOp",EDGE,"E0.sketch_text.stroke-112"),sQuery(id+"F0.wireOp",EDGE,"E0.sketch_text.stroke-113")])],"isStart":false}),makeQuery(id+"F1.opExtrude","CAP_FACE",FACE,{"disambiguationData":[OSD([sQuery(id+"F0.wireOp",EDGE,"E0.sketch_text.stroke-118"),sQuery(id+"F0.wireOp",EDGE,"E0.sketch_text.stroke-119"),sQuery(id+"F0.wireOp",EDGE,"E0.sketch_text.stroke-120"),sQuery(id+"F0.wireOp",EDGE,"E0.sketch_text.stroke-121"),sQuery(id+"F0.wireOp",EDGE,"E0.sketch_text.stroke-122"),sQuery(id+"F0.wireOp",EDGE,"E0.sketch_text.stroke-123"),sQuery(id+"F0.wireOp",EDGE,"E0.sketch_text.stroke-124"),sQuery(id+"F0.wireOp",EDGE,"E0.sketch_text.stroke-125"),sQuery(id+"F0.wireOp",EDGE,"E0.sketch_text.stroke-126"),sQuery(id+"F0.wireOp",EDGE,"E0.sketch_text.stroke-127"),sQuery(id+"F0.wireOp",EDGE,"E0.sketch_text.stroke-128"),sQuery(id+"F0.wireOp",EDGE,"E0.sketch_text.stroke-129"),sQuery(id+"F0.wireOp",EDGE,"E0.sketch_text.stroke-130"),sQuery(id+"F0.wireOp",EDGE,"E0.sketch_text.stroke-131"),sQuery(id+"F0.wireOp",EDGE,"E0.sketch_text.stroke-132"),sQuery(id+"F0.wireOp",EDGE,"E0.sketch_text.stroke-133"),sQuery(id+"F0.wireOp",EDGE,"E0.sketch_text.stroke-134"),sQuery(id+"F0.wireOp",EDGE,"E0.sketch_text.stroke-135"),sQuery(id+"F0.wireOp",EDGE,"E0.sketch_text.stroke-136"),sQuery(id+"F0.wireOp",EDGE,"E0.sketch_text.stroke-137"),sQuery(id+"F0.wireOp",EDGE,"E0.sketch_text.stroke-138"),sQuery(id+"F0.wireOp",EDGE,"E0.sketch_text.stroke-139"),sQuery(id+"F0.wireOp",EDGE,"E0.sketch_text.stroke-140")])],"isStart":false}),makeQuery(id+"F1.opExtrude","CAP_FACE",FACE,{"disambiguationData":[OSD([sQuery(id+"F0.wireOp",EDGE,"E0.sketch_text.stroke-141"),sQuery(id+"F0.wireOp",EDGE,"E0.sketch_text.stroke-142"),sQuery(id+"F0.wireOp",EDGE,"E0.sketch_text.stroke-143"),sQuery(id+"F0.wireOp",EDGE,"E0.sketch_text.stroke-144"),sQuery(id+"F0.wireOp",EDGE,"E0.sketch_text.stroke-145"),sQuery(id+"F0.wireOp",EDGE,"E0.sketch_text.stroke-146"),sQuery(id+"F0.wireOp",EDGE,"E0.sketch_text.stroke-147"),sQuery(id+"F0.wireOp",EDGE,"E0.sketch_text.stroke-148"),sQuery(id+"F0.wireOp",EDGE,"E0.sketch_text.stroke-149"),sQuery(id+"F0.wireOp",EDGE,"E0.sketch_text.stroke-150"),sQuery(id+"F0.wireOp",EDGE,"E0.sketch_text.stroke-151"),sQuery(id+"F0.wireOp",EDGE,"E0.sketch_text.stroke-152"),sQuery(id+"F0.wireOp",EDGE,"E0.sketch_text.stroke-153"),sQuery(id+"F0.wireOp",EDGE,"E0.sketch_text.stroke-154"),sQuery(id+"F0.wireOp",EDGE,"E0.sketch_text.stroke-155"),sQuery(id+"F0.wireOp",EDGE,"E0.sketch_text.stroke-156"),sQuery(id+"F0.wireOp",EDGE,"E0.sketch_text.stroke-157"),sQuery(id+"F0.wireOp",EDGE,"E0.sketch_text.stroke-158"),sQuery(id+"F0.wireOp",EDGE,"E0.sketch_text.stroke-159"),sQuery(id+"F0.wireOp",EDGE,"E0.sketch_text.stroke-160"),sQuery(id+"F0.wireOp",EDGE,"E0.sketch_text.stroke-161"),sQuery(id+"F0.wireOp",EDGE,"E0.sketch_text.stroke-162"),sQuery(id+"F0.wireOp",EDGE,"E0.sketch_text.stroke-163"),sQuery(id+"F0.wireOp",EDGE,"E0.sketch_text.stroke-164"),sQuery(id+"F0.wireOp",EDGE,"E0.sketch_text.stroke-165"),sQuery(id+"F0.wireOp",EDGE,"E0.sketch_text.stroke-166"),sQuery(id+"F0.wireOp",EDGE,"E0.sketch_text.stroke-167"),sQuery(id+"F0.wireOp",EDGE,"E0.sketch_text.stroke-168"),sQuery(id+"F0.wireOp",EDGE,"E0.sketch_text.stroke-169"),sQuery(id+"F0.wireOp",EDGE,"E0.sketch_text.stroke-170"),sQuery(id+"F0.wireOp",EDGE,"E0.sketch_text.stroke-171"),sQuery(id+"F0.wireOp",EDGE,"E0.sketch_text.stroke-172"),sQuery(id+"F0.wireOp",EDGE,"E0.sketch_text.stroke-173"),sQuery(id+"F0.wireOp",EDGE,"E0.sketch_text.stroke-174"),sQuery(id+"F0.wireOp",EDGE,"E0.sketch_text.stroke-175")])],"isStart":false}),makeQuery(id+"F3.opExtrude","SWEPT_FACE",FACE,{"disambiguationData":[OSD([sQuery(id+"F2.wireOp",EDGE,"E1.bottom")])]})]});
            var sketch = newSketch(context, id + "F8", { "sketchPlane" : qUnion([Q0])});
            skLineSegment(sketch, "E4", {"start": v(-94.5, 68.14) * mm, "end": v(-72.02, 59.41) * mm});
            skLineSegment(sketch, "E5", {"start": v(-72.02, 59.41) * mm, "end": v(-73.63, 41.15) * mm});
            skLineSegment(sketch, "E6", {"start": v(-73.63, 41.15) * mm, "end": v(-83.75, 29.02) * mm});
            skLineSegment(sketch, "E7", {"start": v(-83.75, 29.02) * mm, "end": v(-95.46, 30) * mm});
            skLineSegment(sketch, "E8", {"start": v(-95.46, 30) * mm, "end": v(-94.5, 68.14) * mm});
            skSolve(sketch);
        }
        {
            var Q0;
            Q0 = qSketchRegion(id + "F8", true);
            extrude(context, id + "F9", {"entities" : qUnion([Q0]), "operationType" : NewBodyOperationType.REMOVE, "endBound" : BoundingType.THROUGH_ALL, "oppositeDirection" : true, "depth" : 25.4 * mm});
        }
        {
            var Q0;
            Q0=makeQuery(id+"F3.boolean.opBoolean","MERGE",FACE,{"derivedFrom":[makeQuery(id+"F1.opExtrude","CAP_FACE",FACE,{"disambiguationData":[OSD([sQuery(id+"F0.wireOp",EDGE,"E0.sketch_text.stroke-0"),sQuery(id+"F0.wireOp",EDGE,"E0.sketch_text.stroke-1"),sQuery(id+"F0.wireOp",EDGE,"E0.sketch_text.stroke-2"),sQuery(id+"F0.wireOp",EDGE,"E0.sketch_text.stroke-3"),sQuery(id+"F0.wireOp",EDGE,"E0.sketch_text.stroke-4"),sQuery(id+"F0.wireOp",EDGE,"E0.sketch_text.stroke-5"),sQuery(id+"F0.wireOp",EDGE,"E0.sketch_text.stroke-6"),sQuery(id+"F0.wireOp",EDGE,"E0.sketch_text.stroke-7"),sQuery(id+"F0.wireOp",EDGE,"E0.sketch_text.stroke-8"),sQuery(id+"F0.wireOp",EDGE,"E0.sketch_text.stroke-9"),sQuery(id+"F0.wireOp",EDGE,"E0.sketch_text.stroke-10"),sQuery(id+"F0.wireOp",EDGE,"E0.sketch_text.stroke-11"),sQuery(id+"F0.wireOp",EDGE,"E0.sketch_text.stroke-12"),sQuery(id+"F0.wireOp",EDGE,"E0.sketch_text.stroke-13"),sQuery(id+"F0.wireOp",EDGE,"E0.sketch_text.stroke-14"),sQuery(id+"F0.wireOp",EDGE,"E0.sketch_text.stroke-15"),sQuery(id+"F0.wireOp",EDGE,"E0.sketch_text.stroke-16"),sQuery(id+"F0.wireOp",EDGE,"E0.sketch_text.stroke-17"),sQuery(id+"F0.wireOp",EDGE,"E0.sketch_text.stroke-18"),sQuery(id+"F0.wireOp",EDGE,"E0.sketch_text.stroke-19")])],"isStart":false}),makeQuery(id+"F1.opExtrude","CAP_FACE",FACE,{"disambiguationData":[OSD([sQuery(id+"F0.wireOp",EDGE,"E0.sketch_text.stroke-20"),sQuery(id+"F0.wireOp",EDGE,"E0.sketch_text.stroke-21"),sQuery(id+"F0.wireOp",EDGE,"E0.sketch_text.stroke-22"),sQuery(id+"F0.wireOp",EDGE,"E0.sketch_text.stroke-23"),sQuery(id+"F0.wireOp",EDGE,"E0.sketch_text.stroke-24"),sQuery(id+"F0.wireOp",EDGE,"E0.sketch_text.stroke-25"),sQuery(id+"F0.wireOp",EDGE,"E0.sketch_text.stroke-26"),sQuery(id+"F0.wireOp",EDGE,"E0.sketch_text.stroke-27"),sQuery(id+"F0.wireOp",EDGE,"E0.sketch_text.stroke-28"),sQuery(id+"F0.wireOp",EDGE,"E0.sketch_text.stroke-29"),sQuery(id+"F0.wireOp",EDGE,"E0.sketch_text.stroke-30"),sQuery(id+"F0.wireOp",EDGE,"E0.sketch_text.stroke-31"),sQuery(id+"F0.wireOp",EDGE,"E0.sketch_text.stroke-32"),sQuery(id+"F0.wireOp",EDGE,"E0.sketch_text.stroke-33"),sQuery(id+"F0.wireOp",EDGE,"E0.sketch_text.stroke-34"),sQuery(id+"F0.wireOp",EDGE,"E0.sketch_text.stroke-35"),sQuery(id+"F0.wireOp",EDGE,"E0.sketch_text.stroke-36"),sQuery(id+"F0.wireOp",EDGE,"E0.sketch_text.stroke-37"),sQuery(id+"F0.wireOp",EDGE,"E0.sketch_text.stroke-38"),sQuery(id+"F0.wireOp",EDGE,"E0.sketch_text.stroke-39"),sQuery(id+"F0.wireOp",EDGE,"E0.sketch_text.stroke-40"),sQuery(id+"F0.wireOp",EDGE,"E0.sketch_text.stroke-41"),sQuery(id+"F0.wireOp",EDGE,"E0.sketch_text.stroke-42"),sQuery(id+"F0.wireOp",EDGE,"E0.sketch_text.stroke-43"),sQuery(id+"F0.wireOp",EDGE,"E0.sketch_text.stroke-44"),sQuery(id+"F0.wireOp",EDGE,"E0.sketch_text.stroke-45"),sQuery(id+"F0.wireOp",EDGE,"E0.sketch_text.stroke-46"),sQuery(id+"F0.wireOp",EDGE,"E0.sketch_text.stroke-47"),sQuery(id+"F0.wireOp",EDGE,"E0.sketch_text.stroke-48"),sQuery(id+"F0.wireOp",EDGE,"E0.sketch_text.stroke-49"),sQuery(id+"F0.wireOp",EDGE,"E0.sketch_text.stroke-50"),sQuery(id+"F0.wireOp",EDGE,"E0.sketch_text.stroke-51"),sQuery(id+"F0.wireOp",EDGE,"E0.sketch_text.stroke-52"),sQuery(id+"F0.wireOp",EDGE,"E0.sketch_text.stroke-53"),sQuery(id+"F0.wireOp",EDGE,"E0.sketch_text.stroke-54"),sQuery(id+"F0.wireOp",EDGE,"E0.sketch_text.stroke-55"),sQuery(id+"F0.wireOp",EDGE,"E0.sketch_text.stroke-56"),sQuery(id+"F0.wireOp",EDGE,"E0.sketch_text.stroke-57"),sQuery(id+"F0.wireOp",EDGE,"E0.sketch_text.stroke-58"),sQuery(id+"F0.wireOp",EDGE,"E0.sketch_text.stroke-59"),sQuery(id+"F0.wireOp",EDGE,"E0.sketch_text.stroke-60")])],"isStart":false}),makeQuery(id+"F1.opExtrude","CAP_FACE",FACE,{"disambiguationData":[OSD([sQuery(id+"F0.wireOp",EDGE,"E0.sketch_text.stroke-61"),sQuery(id+"F0.wireOp",EDGE,"E0.sketch_text.stroke-62"),sQuery(id+"F0.wireOp",EDGE,"E0.sketch_text.stroke-63"),sQuery(id+"F0.wireOp",EDGE,"E0.sketch_text.stroke-64"),sQuery(id+"F0.wireOp",EDGE,"E0.sketch_text.stroke-65"),sQuery(id+"F0.wireOp",EDGE,"E0.sketch_text.stroke-66"),sQuery(id+"F0.wireOp",EDGE,"E0.sketch_text.stroke-67"),sQuery(id+"F0.wireOp",EDGE,"E0.sketch_text.stroke-68"),sQuery(id+"F0.wireOp",EDGE,"E0.sketch_text.stroke-69"),sQuery(id+"F0.wireOp",EDGE,"E0.sketch_text.stroke-70"),sQuery(id+"F0.wireOp",EDGE,"E0.sketch_text.stroke-71"),sQuery(id+"F0.wireOp",EDGE,"E0.sketch_text.stroke-72"),sQuery(id+"F0.wireOp",EDGE,"E0.sketch_text.stroke-73"),sQuery(id+"F0.wireOp",EDGE,"E0.sketch_text.stroke-74"),sQuery(id+"F0.wireOp",EDGE,"E0.sketch_text.stroke-75"),sQuery(id+"F0.wireOp",EDGE,"E0.sketch_text.stroke-76"),sQuery(id+"F0.wireOp",EDGE,"E0.sketch_text.stroke-77"),sQuery(id+"F0.wireOp",EDGE,"E0.sketch_text.stroke-78"),sQuery(id+"F0.wireOp",EDGE,"E0.sketch_text.stroke-79"),sQuery(id+"F0.wireOp",EDGE,"E0.sketch_text.stroke-80"),sQuery(id+"F0.wireOp",EDGE,"E0.sketch_text.stroke-81"),sQuery(id+"F0.wireOp",EDGE,"E0.sketch_text.stroke-82"),sQuery(id+"F0.wireOp",EDGE,"E0.sketch_text.stroke-83"),sQuery(id+"F0.wireOp",EDGE,"E0.sketch_text.stroke-84")])],"isStart":false}),makeQuery(id+"F1.opExtrude","CAP_FACE",FACE,{"disambiguationData":[OSD([sQuery(id+"F0.wireOp",EDGE,"E0.sketch_text.stroke-85"),sQuery(id+"F0.wireOp",EDGE,"E0.sketch_text.stroke-86"),sQuery(id+"F0.wireOp",EDGE,"E0.sketch_text.stroke-87"),sQuery(id+"F0.wireOp",EDGE,"E0.sketch_text.stroke-88"),sQuery(id+"F0.wireOp",EDGE,"E0.sketch_text.stroke-89"),sQuery(id+"F0.wireOp",EDGE,"E0.sketch_text.stroke-90"),sQuery(id+"F0.wireOp",EDGE,"E0.sketch_text.stroke-91"),sQuery(id+"F0.wireOp",EDGE,"E0.sketch_text.stroke-92"),sQuery(id+"F0.wireOp",EDGE,"E0.sketch_text.stroke-93"),sQuery(id+"F0.wireOp",EDGE,"E0.sketch_text.stroke-94"),sQuery(id+"F0.wireOp",EDGE,"E0.sketch_text.stroke-95"),sQuery(id+"F0.wireOp",EDGE,"E0.sketch_text.stroke-96"),sQuery(id+"F0.wireOp",EDGE,"E0.sketch_text.stroke-97"),sQuery(id+"F0.wireOp",EDGE,"E0.sketch_text.stroke-98"),sQuery(id+"F0.wireOp",EDGE,"E0.sketch_text.stroke-99"),sQuery(id+"F0.wireOp",EDGE,"E0.sketch_text.stroke-100"),sQuery(id+"F0.wireOp",EDGE,"E0.sketch_text.stroke-101"),sQuery(id+"F0.wireOp",EDGE,"E0.sketch_text.stroke-102"),sQuery(id+"F0.wireOp",EDGE,"E0.sketch_text.stroke-103")])],"isStart":false}),makeQuery(id+"F1.opExtrude","CAP_FACE",FACE,{"disambiguationData":[OSD([sQuery(id+"F0.wireOp",EDGE,"E0.sketch_text.stroke-104"),sQuery(id+"F0.wireOp",EDGE,"E0.sketch_text.stroke-105"),sQuery(id+"F0.wireOp",EDGE,"E0.sketch_text.stroke-106"),sQuery(id+"F0.wireOp",EDGE,"E0.sketch_text.stroke-107"),sQuery(id+"F0.wireOp",EDGE,"E0.sketch_text.stroke-108"),sQuery(id+"F0.wireOp",EDGE,"E0.sketch_text.stroke-109"),sQuery(id+"F0.wireOp",EDGE,"E0.sketch_text.stroke-110"),sQuery(id+"F0.wireOp",EDGE,"E0.sketch_text.stroke-111"),sQuery(id+"F0.wireOp",EDGE,"E0.sketch_text.stroke-112"),sQuery(id+"F0.wireOp",EDGE,"E0.sketch_text.stroke-113")])],"isStart":false}),makeQuery(id+"F1.opExtrude","CAP_FACE",FACE,{"disambiguationData":[OSD([sQuery(id+"F0.wireOp",EDGE,"E0.sketch_text.stroke-118"),sQuery(id+"F0.wireOp",EDGE,"E0.sketch_text.stroke-119"),sQuery(id+"F0.wireOp",EDGE,"E0.sketch_text.stroke-120"),sQuery(id+"F0.wireOp",EDGE,"E0.sketch_text.stroke-121"),sQuery(id+"F0.wireOp",EDGE,"E0.sketch_text.stroke-122"),sQuery(id+"F0.wireOp",EDGE,"E0.sketch_text.stroke-123"),sQuery(id+"F0.wireOp",EDGE,"E0.sketch_text.stroke-124"),sQuery(id+"F0.wireOp",EDGE,"E0.sketch_text.stroke-125"),sQuery(id+"F0.wireOp",EDGE,"E0.sketch_text.stroke-126"),sQuery(id+"F0.wireOp",EDGE,"E0.sketch_text.stroke-127"),sQuery(id+"F0.wireOp",EDGE,"E0.sketch_text.stroke-128"),sQuery(id+"F0.wireOp",EDGE,"E0.sketch_text.stroke-129"),sQuery(id+"F0.wireOp",EDGE,"E0.sketch_text.stroke-130"),sQuery(id+"F0.wireOp",EDGE,"E0.sketch_text.stroke-131"),sQuery(id+"F0.wireOp",EDGE,"E0.sketch_text.stroke-132"),sQuery(id+"F0.wireOp",EDGE,"E0.sketch_text.stroke-133"),sQuery(id+"F0.wireOp",EDGE,"E0.sketch_text.stroke-134"),sQuery(id+"F0.wireOp",EDGE,"E0.sketch_text.stroke-135"),sQuery(id+"F0.wireOp",EDGE,"E0.sketch_text.stroke-136"),sQuery(id+"F0.wireOp",EDGE,"E0.sketch_text.stroke-137"),sQuery(id+"F0.wireOp",EDGE,"E0.sketch_text.stroke-138"),sQuery(id+"F0.wireOp",EDGE,"E0.sketch_text.stroke-139"),sQuery(id+"F0.wireOp",EDGE,"E0.sketch_text.stroke-140")])],"isStart":false}),makeQuery(id+"F1.opExtrude","CAP_FACE",FACE,{"disambiguationData":[OSD([sQuery(id+"F0.wireOp",EDGE,"E0.sketch_text.stroke-141"),sQuery(id+"F0.wireOp",EDGE,"E0.sketch_text.stroke-142"),sQuery(id+"F0.wireOp",EDGE,"E0.sketch_text.stroke-143"),sQuery(id+"F0.wireOp",EDGE,"E0.sketch_text.stroke-144"),sQuery(id+"F0.wireOp",EDGE,"E0.sketch_text.stroke-145"),sQuery(id+"F0.wireOp",EDGE,"E0.sketch_text.stroke-146"),sQuery(id+"F0.wireOp",EDGE,"E0.sketch_text.stroke-147"),sQuery(id+"F0.wireOp",EDGE,"E0.sketch_text.stroke-148"),sQuery(id+"F0.wireOp",EDGE,"E0.sketch_text.stroke-149"),sQuery(id+"F0.wireOp",EDGE,"E0.sketch_text.stroke-150"),sQuery(id+"F0.wireOp",EDGE,"E0.sketch_text.stroke-151"),sQuery(id+"F0.wireOp",EDGE,"E0.sketch_text.stroke-152"),sQuery(id+"F0.wireOp",EDGE,"E0.sketch_text.stroke-153"),sQuery(id+"F0.wireOp",EDGE,"E0.sketch_text.stroke-154"),sQuery(id+"F0.wireOp",EDGE,"E0.sketch_text.stroke-155"),sQuery(id+"F0.wireOp",EDGE,"E0.sketch_text.stroke-156"),sQuery(id+"F0.wireOp",EDGE,"E0.sketch_text.stroke-157"),sQuery(id+"F0.wireOp",EDGE,"E0.sketch_text.stroke-158"),sQuery(id+"F0.wireOp",EDGE,"E0.sketch_text.stroke-159"),sQuery(id+"F0.wireOp",EDGE,"E0.sketch_text.stroke-160"),sQuery(id+"F0.wireOp",EDGE,"E0.sketch_text.stroke-161"),sQuery(id+"F0.wireOp",EDGE,"E0.sketch_text.stroke-162"),sQuery(id+"F0.wireOp",EDGE,"E0.sketch_text.stroke-163"),sQuery(id+"F0.wireOp",EDGE,"E0.sketch_text.stroke-164"),sQuery(id+"F0.wireOp",EDGE,"E0.sketch_text.stroke-165"),sQuery(id+"F0.wireOp",EDGE,"E0.sketch_text.stroke-166"),sQuery(id+"F0.wireOp",EDGE,"E0.sketch_text.stroke-167"),sQuery(id+"F0.wireOp",EDGE,"E0.sketch_text.stroke-168"),sQuery(id+"F0.wireOp",EDGE,"E0.sketch_text.stroke-169"),sQuery(id+"F0.wireOp",EDGE,"E0.sketch_text.stroke-170"),sQuery(id+"F0.wireOp",EDGE,"E0.sketch_text.stroke-171"),sQuery(id+"F0.wireOp",EDGE,"E0.sketch_text.stroke-172"),sQuery(id+"F0.wireOp",EDGE,"E0.sketch_text.stroke-173"),sQuery(id+"F0.wireOp",EDGE,"E0.sketch_text.stroke-174"),sQuery(id+"F0.wireOp",EDGE,"E0.sketch_text.stroke-175")])],"isStart":false}),makeQuery(id+"F3.opExtrude","SWEPT_FACE",FACE,{"disambiguationData":[OSD([sQuery(id+"F2.wireOp",EDGE,"E1.bottom")])]})]});
            var sketch = newSketch(context, id + "F10", { "sketchPlane" : qUnion([Q0])});
            skArc(sketch, "E9", {"start": v(-76.98, 52.4) * mm, "mid": v(-86.38, 42.09) * mm, "end": v(-92.98, 29.8) * mm});
            skArc(sketch, "E10", {"start": v(-72.03, 45.55) * mm, "mid": v(-79.04, 38.1) * mm, "end": v(-83.75, 29.02) * mm});
            skLineSegment(sketch, "E11", {"start": v(-76.98, 52.4) * mm, "end": v(-72.03, 45.55) * mm});
            skLineSegment(sketch, "E12", {"start": v(-92.98, 29.8) * mm, "end": v(-83.75, 29.02) * mm});
            skSolve(sketch);
        }
        {
            var Q0;
            Q0 = qSketchRegion(id + "F10", true);
            extrude(context, id + "F11", {"entities" : qUnion([Q0]), "operationType" : NewBodyOperationType.ADD, "oppositeDirection" : true, "depth" : 25.4 * mm});
        }
        {
            var Q0;
            Q0=makeQuery(id+"F11.boolean.opBoolean","MERGE",FACE,{"derivedFrom":[makeQuery(id+"F3.boolean.opBoolean","MERGE",FACE,{"derivedFrom":[makeQuery(id+"F1.opExtrude","CAP_FACE",FACE,{"disambiguationData":[OSD([sQuery(id+"F0.wireOp",EDGE,"E0.sketch_text.stroke-0"),sQuery(id+"F0.wireOp",EDGE,"E0.sketch_text.stroke-1"),sQuery(id+"F0.wireOp",EDGE,"E0.sketch_text.stroke-2"),sQuery(id+"F0.wireOp",EDGE,"E0.sketch_text.stroke-3"),sQuery(id+"F0.wireOp",EDGE,"E0.sketch_text.stroke-4"),sQuery(id+"F0.wireOp",EDGE,"E0.sketch_text.stroke-5"),sQuery(id+"F0.wireOp",EDGE,"E0.sketch_text.stroke-6"),sQuery(id+"F0.wireOp",EDGE,"E0.sketch_text.stroke-7"),sQuery(id+"F0.wireOp",EDGE,"E0.sketch_text.stroke-8"),sQuery(id+"F0.wireOp",EDGE,"E0.sketch_text.stroke-9"),sQuery(id+"F0.wireOp",EDGE,"E0.sketch_text.stroke-10"),sQuery(id+"F0.wireOp",EDGE,"E0.sketch_text.stroke-11"),sQuery(id+"F0.wireOp",EDGE,"E0.sketch_text.stroke-12"),sQuery(id+"F0.wireOp",EDGE,"E0.sketch_text.stroke-13"),sQuery(id+"F0.wireOp",EDGE,"E0.sketch_text.stroke-14"),sQuery(id+"F0.wireOp",EDGE,"E0.sketch_text.stroke-15"),sQuery(id+"F0.wireOp",EDGE,"E0.sketch_text.stroke-16"),sQuery(id+"F0.wireOp",EDGE,"E0.sketch_text.stroke-17"),sQuery(id+"F0.wireOp",EDGE,"E0.sketch_text.stroke-18"),sQuery(id+"F0.wireOp",EDGE,"E0.sketch_text.stroke-19")])],"isStart":false}),makeQuery(id+"F1.opExtrude","CAP_FACE",FACE,{"disambiguationData":[OSD([sQuery(id+"F0.wireOp",EDGE,"E0.sketch_text.stroke-20"),sQuery(id+"F0.wireOp",EDGE,"E0.sketch_text.stroke-21"),sQuery(id+"F0.wireOp",EDGE,"E0.sketch_text.stroke-22"),sQuery(id+"F0.wireOp",EDGE,"E0.sketch_text.stroke-23"),sQuery(id+"F0.wireOp",EDGE,"E0.sketch_text.stroke-24"),sQuery(id+"F0.wireOp",EDGE,"E0.sketch_text.stroke-25"),sQuery(id+"F0.wireOp",EDGE,"E0.sketch_text.stroke-26"),sQuery(id+"F0.wireOp",EDGE,"E0.sketch_text.stroke-27"),sQuery(id+"F0.wireOp",EDGE,"E0.sketch_text.stroke-28"),sQuery(id+"F0.wireOp",EDGE,"E0.sketch_text.stroke-29"),sQuery(id+"F0.wireOp",EDGE,"E0.sketch_text.stroke-30"),sQuery(id+"F0.wireOp",EDGE,"E0.sketch_text.stroke-31"),sQuery(id+"F0.wireOp",EDGE,"E0.sketch_text.stroke-32"),sQuery(id+"F0.wireOp",EDGE,"E0.sketch_text.stroke-33"),sQuery(id+"F0.wireOp",EDGE,"E0.sketch_text.stroke-34"),sQuery(id+"F0.wireOp",EDGE,"E0.sketch_text.stroke-35"),sQuery(id+"F0.wireOp",EDGE,"E0.sketch_text.stroke-36"),sQuery(id+"F0.wireOp",EDGE,"E0.sketch_text.stroke-37"),sQuery(id+"F0.wireOp",EDGE,"E0.sketch_text.stroke-38"),sQuery(id+"F0.wireOp",EDGE,"E0.sketch_text.stroke-39"),sQuery(id+"F0.wireOp",EDGE,"E0.sketch_text.stroke-40"),sQuery(id+"F0.wireOp",EDGE,"E0.sketch_text.stroke-41"),sQuery(id+"F0.wireOp",EDGE,"E0.sketch_text.stroke-42"),sQuery(id+"F0.wireOp",EDGE,"E0.sketch_text.stroke-43"),sQuery(id+"F0.wireOp",EDGE,"E0.sketch_text.stroke-44"),sQuery(id+"F0.wireOp",EDGE,"E0.sketch_text.stroke-45"),sQuery(id+"F0.wireOp",EDGE,"E0.sketch_text.stroke-46"),sQuery(id+"F0.wireOp",EDGE,"E0.sketch_text.stroke-47"),sQuery(id+"F0.wireOp",EDGE,"E0.sketch_text.stroke-48"),sQuery(id+"F0.wireOp",EDGE,"E0.sketch_text.stroke-49"),sQuery(id+"F0.wireOp",EDGE,"E0.sketch_text.stroke-50"),sQuery(id+"F0.wireOp",EDGE,"E0.sketch_text.stroke-51"),sQuery(id+"F0.wireOp",EDGE,"E0.sketch_text.stroke-52"),sQuery(id+"F0.wireOp",EDGE,"E0.sketch_text.stroke-53"),sQuery(id+"F0.wireOp",EDGE,"E0.sketch_text.stroke-54"),sQuery(id+"F0.wireOp",EDGE,"E0.sketch_text.stroke-55"),sQuery(id+"F0.wireOp",EDGE,"E0.sketch_text.stroke-56"),sQuery(id+"F0.wireOp",EDGE,"E0.sketch_text.stroke-57"),sQuery(id+"F0.wireOp",EDGE,"E0.sketch_text.stroke-58"),sQuery(id+"F0.wireOp",EDGE,"E0.sketch_text.stroke-59"),sQuery(id+"F0.wireOp",EDGE,"E0.sketch_text.stroke-60")])],"isStart":false}),makeQuery(id+"F1.opExtrude","CAP_FACE",FACE,{"disambiguationData":[OSD([sQuery(id+"F0.wireOp",EDGE,"E0.sketch_text.stroke-61"),sQuery(id+"F0.wireOp",EDGE,"E0.sketch_text.stroke-62"),sQuery(id+"F0.wireOp",EDGE,"E0.sketch_text.stroke-63"),sQuery(id+"F0.wireOp",EDGE,"E0.sketch_text.stroke-64"),sQuery(id+"F0.wireOp",EDGE,"E0.sketch_text.stroke-65"),sQuery(id+"F0.wireOp",EDGE,"E0.sketch_text.stroke-66"),sQuery(id+"F0.wireOp",EDGE,"E0.sketch_text.stroke-67"),sQuery(id+"F0.wireOp",EDGE,"E0.sketch_text.stroke-68"),sQuery(id+"F0.wireOp",EDGE,"E0.sketch_text.stroke-69"),sQuery(id+"F0.wireOp",EDGE,"E0.sketch_text.stroke-70"),sQuery(id+"F0.wireOp",EDGE,"E0.sketch_text.stroke-71"),sQuery(id+"F0.wireOp",EDGE,"E0.sketch_text.stroke-72"),sQuery(id+"F0.wireOp",EDGE,"E0.sketch_text.stroke-73"),sQuery(id+"F0.wireOp",EDGE,"E0.sketch_text.stroke-74"),sQuery(id+"F0.wireOp",EDGE,"E0.sketch_text.stroke-75"),sQuery(id+"F0.wireOp",EDGE,"E0.sketch_text.stroke-76"),sQuery(id+"F0.wireOp",EDGE,"E0.sketch_text.stroke-77"),sQuery(id+"F0.wireOp",EDGE,"E0.sketch_text.stroke-78"),sQuery(id+"F0.wireOp",EDGE,"E0.sketch_text.stroke-79"),sQuery(id+"F0.wireOp",EDGE,"E0.sketch_text.stroke-80"),sQuery(id+"F0.wireOp",EDGE,"E0.sketch_text.stroke-81"),sQuery(id+"F0.wireOp",EDGE,"E0.sketch_text.stroke-82"),sQuery(id+"F0.wireOp",EDGE,"E0.sketch_text.stroke-83"),sQuery(id+"F0.wireOp",EDGE,"E0.sketch_text.stroke-84")])],"isStart":false}),makeQuery(id+"F1.opExtrude","CAP_FACE",FACE,{"disambiguationData":[OSD([sQuery(id+"F0.wireOp",EDGE,"E0.sketch_text.stroke-85"),sQuery(id+"F0.wireOp",EDGE,"E0.sketch_text.stroke-86"),sQuery(id+"F0.wireOp",EDGE,"E0.sketch_text.stroke-87"),sQuery(id+"F0.wireOp",EDGE,"E0.sketch_text.stroke-88"),sQuery(id+"F0.wireOp",EDGE,"E0.sketch_text.stroke-89"),sQuery(id+"F0.wireOp",EDGE,"E0.sketch_text.stroke-90"),sQuery(id+"F0.wireOp",EDGE,"E0.sketch_text.stroke-91"),sQuery(id+"F0.wireOp",EDGE,"E0.sketch_text.stroke-92"),sQuery(id+"F0.wireOp",EDGE,"E0.sketch_text.stroke-93"),sQuery(id+"F0.wireOp",EDGE,"E0.sketch_text.stroke-94"),sQuery(id+"F0.wireOp",EDGE,"E0.sketch_text.stroke-95"),sQuery(id+"F0.wireOp",EDGE,"E0.sketch_text.stroke-96"),sQuery(id+"F0.wireOp",EDGE,"E0.sketch_text.stroke-97"),sQuery(id+"F0.wireOp",EDGE,"E0.sketch_text.stroke-98"),sQuery(id+"F0.wireOp",EDGE,"E0.sketch_text.stroke-99"),sQuery(id+"F0.wireOp",EDGE,"E0.sketch_text.stroke-100"),sQuery(id+"F0.wireOp",EDGE,"E0.sketch_text.stroke-101"),sQuery(id+"F0.wireOp",EDGE,"E0.sketch_text.stroke-102"),sQuery(id+"F0.wireOp",EDGE,"E0.sketch_text.stroke-103")])],"isStart":false}),makeQuery(id+"F1.opExtrude","CAP_FACE",FACE,{"disambiguationData":[OSD([sQuery(id+"F0.wireOp",EDGE,"E0.sketch_text.stroke-104"),sQuery(id+"F0.wireOp",EDGE,"E0.sketch_text.stroke-105"),sQuery(id+"F0.wireOp",EDGE,"E0.sketch_text.stroke-106"),sQuery(id+"F0.wireOp",EDGE,"E0.sketch_text.stroke-107"),sQuery(id+"F0.wireOp",EDGE,"E0.sketch_text.stroke-108"),sQuery(id+"F0.wireOp",EDGE,"E0.sketch_text.stroke-109"),sQuery(id+"F0.wireOp",EDGE,"E0.sketch_text.stroke-110"),sQuery(id+"F0.wireOp",EDGE,"E0.sketch_text.stroke-111"),sQuery(id+"F0.wireOp",EDGE,"E0.sketch_text.stroke-112"),sQuery(id+"F0.wireOp",EDGE,"E0.sketch_text.stroke-113")])],"isStart":false}),makeQuery(id+"F1.opExtrude","CAP_FACE",FACE,{"disambiguationData":[OSD([sQuery(id+"F0.wireOp",EDGE,"E0.sketch_text.stroke-118"),sQuery(id+"F0.wireOp",EDGE,"E0.sketch_text.stroke-119"),sQuery(id+"F0.wireOp",EDGE,"E0.sketch_text.stroke-120"),sQuery(id+"F0.wireOp",EDGE,"E0.sketch_text.stroke-121"),sQuery(id+"F0.wireOp",EDGE,"E0.sketch_text.stroke-122"),sQuery(id+"F0.wireOp",EDGE,"E0.sketch_text.stroke-123"),sQuery(id+"F0.wireOp",EDGE,"E0.sketch_text.stroke-124"),sQuery(id+"F0.wireOp",EDGE,"E0.sketch_text.stroke-125"),sQuery(id+"F0.wireOp",EDGE,"E0.sketch_text.stroke-126"),sQuery(id+"F0.wireOp",EDGE,"E0.sketch_text.stroke-127"),sQuery(id+"F0.wireOp",EDGE,"E0.sketch_text.stroke-128"),sQuery(id+"F0.wireOp",EDGE,"E0.sketch_text.stroke-129"),sQuery(id+"F0.wireOp",EDGE,"E0.sketch_text.stroke-130"),sQuery(id+"F0.wireOp",EDGE,"E0.sketch_text.stroke-131"),sQuery(id+"F0.wireOp",EDGE,"E0.sketch_text.stroke-132"),sQuery(id+"F0.wireOp",EDGE,"E0.sketch_text.stroke-133"),sQuery(id+"F0.wireOp",EDGE,"E0.sketch_text.stroke-134"),sQuery(id+"F0.wireOp",EDGE,"E0.sketch_text.stroke-135"),sQuery(id+"F0.wireOp",EDGE,"E0.sketch_text.stroke-136"),sQuery(id+"F0.wireOp",EDGE,"E0.sketch_text.stroke-137"),sQuery(id+"F0.wireOp",EDGE,"E0.sketch_text.stroke-138"),sQuery(id+"F0.wireOp",EDGE,"E0.sketch_text.stroke-139"),sQuery(id+"F0.wireOp",EDGE,"E0.sketch_text.stroke-140")])],"isStart":false}),makeQuery(id+"F1.opExtrude","CAP_FACE",FACE,{"disambiguationData":[OSD([sQuery(id+"F0.wireOp",EDGE,"E0.sketch_text.stroke-141"),sQuery(id+"F0.wireOp",EDGE,"E0.sketch_text.stroke-142"),sQuery(id+"F0.wireOp",EDGE,"E0.sketch_text.stroke-143"),sQuery(id+"F0.wireOp",EDGE,"E0.sketch_text.stroke-144"),sQuery(id+"F0.wireOp",EDGE,"E0.sketch_text.stroke-145"),sQuery(id+"F0.wireOp",EDGE,"E0.sketch_text.stroke-146"),sQuery(id+"F0.wireOp",EDGE,"E0.sketch_text.stroke-147"),sQuery(id+"F0.wireOp",EDGE,"E0.sketch_text.stroke-148"),sQuery(id+"F0.wireOp",EDGE,"E0.sketch_text.stroke-149"),sQuery(id+"F0.wireOp",EDGE,"E0.sketch_text.stroke-150"),sQuery(id+"F0.wireOp",EDGE,"E0.sketch_text.stroke-151"),sQuery(id+"F0.wireOp",EDGE,"E0.sketch_text.stroke-152"),sQuery(id+"F0.wireOp",EDGE,"E0.sketch_text.stroke-153"),sQuery(id+"F0.wireOp",EDGE,"E0.sketch_text.stroke-154"),sQuery(id+"F0.wireOp",EDGE,"E0.sketch_text.stroke-155"),sQuery(id+"F0.wireOp",EDGE,"E0.sketch_text.stroke-156"),sQuery(id+"F0.wireOp",EDGE,"E0.sketch_text.stroke-157"),sQuery(id+"F0.wireOp",EDGE,"E0.sketch_text.stroke-158"),sQuery(id+"F0.wireOp",EDGE,"E0.sketch_text.stroke-159"),sQuery(id+"F0.wireOp",EDGE,"E0.sketch_text.stroke-160"),sQuery(id+"F0.wireOp",EDGE,"E0.sketch_text.stroke-161"),sQuery(id+"F0.wireOp",EDGE,"E0.sketch_text.stroke-162"),sQuery(id+"F0.wireOp",EDGE,"E0.sketch_text.stroke-163"),sQuery(id+"F0.wireOp",EDGE,"E0.sketch_text.stroke-164"),sQuery(id+"F0.wireOp",EDGE,"E0.sketch_text.stroke-165"),sQuery(id+"F0.wireOp",EDGE,"E0.sketch_text.stroke-166"),sQuery(id+"F0.wireOp",EDGE,"E0.sketch_text.stroke-167"),sQuery(id+"F0.wireOp",EDGE,"E0.sketch_text.stroke-168"),sQuery(id+"F0.wireOp",EDGE,"E0.sketch_text.stroke-169"),sQuery(id+"F0.wireOp",EDGE,"E0.sketch_text.stroke-170"),sQuery(id+"F0.wireOp",EDGE,"E0.sketch_text.stroke-171"),sQuery(id+"F0.wireOp",EDGE,"E0.sketch_text.stroke-172"),sQuery(id+"F0.wireOp",EDGE,"E0.sketch_text.stroke-173"),sQuery(id+"F0.wireOp",EDGE,"E0.sketch_text.stroke-174"),sQuery(id+"F0.wireOp",EDGE,"E0.sketch_text.stroke-175")])],"isStart":false}),makeQuery(id+"F3.opExtrude","SWEPT_FACE",FACE,{"disambiguationData":[OSD([sQuery(id+"F2.wireOp",EDGE,"E1.bottom")])]})]}),makeQuery(id+"F11.opExtrude","CAP_FACE",FACE,{"disambiguationData":[OSD([sQuery(id+"F10.wireOp",EDGE,"E9"),sQuery(id+"F10.wireOp",EDGE,"E10"),sQuery(id+"F10.wireOp",EDGE,"E11"),sQuery(id+"F10.wireOp",EDGE,"E12")])],"isStart":true})]});
            var sketch = newSketch(context, id + "F12", { "sketchPlane" : qUnion([Q0])});
            skFitSpline(sketch, "E13", {"points": [v(274.25, 17.5) * mm, v(276.01, 39.68) * mm, v(283.4, 18.2) * mm, v(274.25, 17.5) * mm]});
            skSolve(sketch);
        }
        {
            var Q0;
            Q0 = qSketchRegion(id + "F12", true);
            extrude(context, id + "F13", {"entities" : qUnion([Q0]), "operationType" : NewBodyOperationType.REMOVE, "endBound" : BoundingType.THROUGH_ALL, "oppositeDirection" : true, "depth" : 25.4 * mm});
        }
    });
